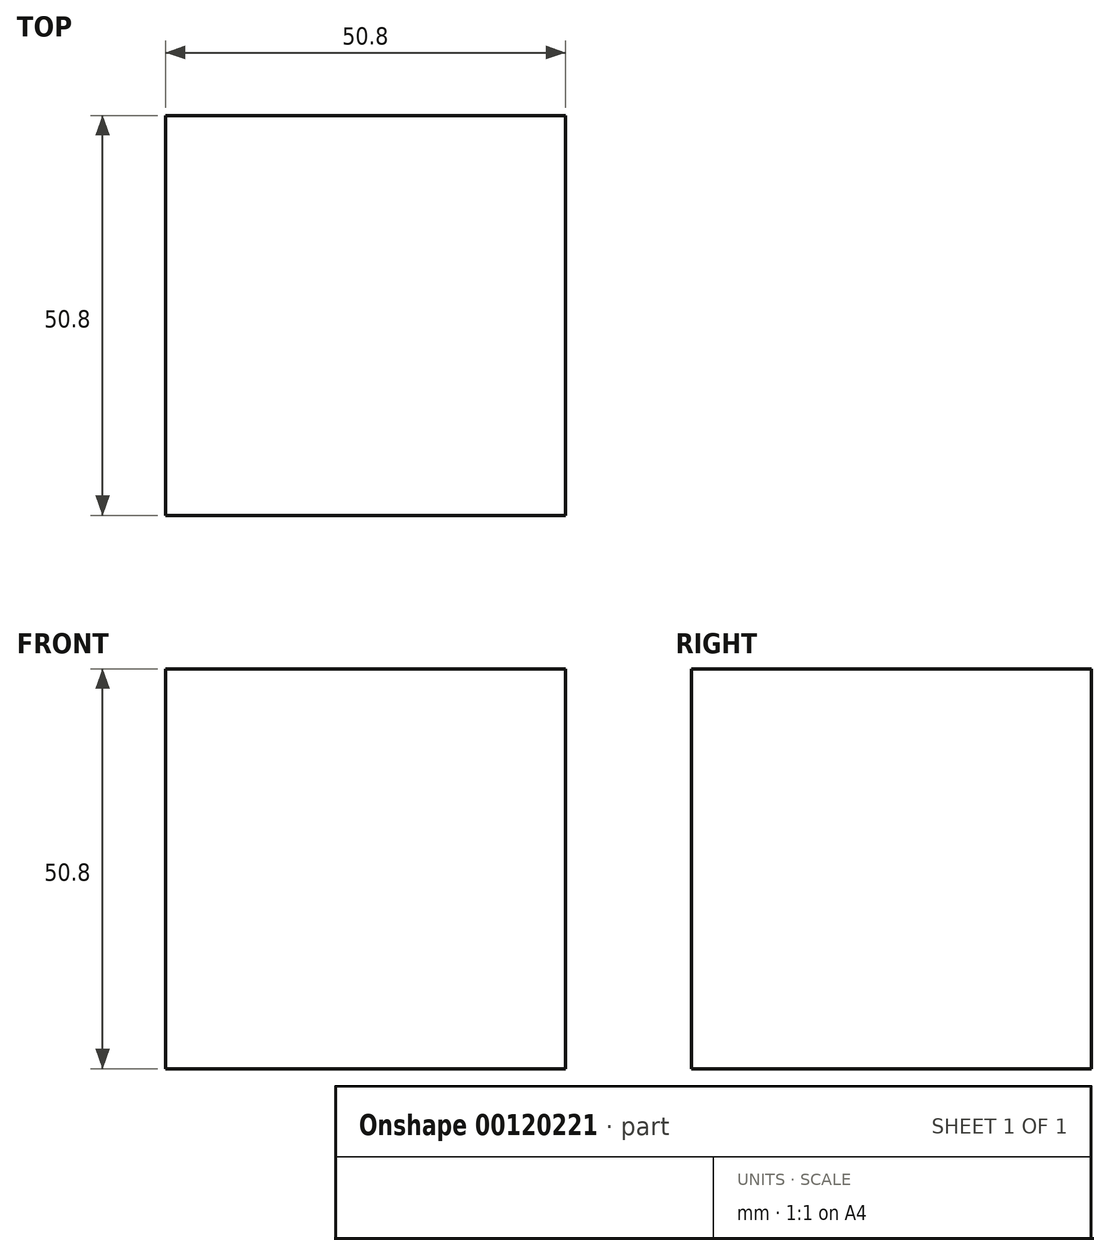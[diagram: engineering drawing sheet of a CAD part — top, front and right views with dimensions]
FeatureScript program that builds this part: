
annotation { "Feature Type Name" : "Feature", "Feature Type Description" : "" }
export const myFeature = defineFeature(function(context is Context, id is Id, definition is map)
    precondition{}
    {
        {
            var Q0;
            Q0=qCreatedBy(makeId("Top.planeOp"),FACE);
            var sketch = newSketch(context, id + "F0", { "sketchPlane" : qUnion([Q0])});
            skLineSegment(sketch, "E0.bottom", {"start": v(-20.33, 28.96) * mm, "end": v(30.47, 28.96) * mm});
            skLineSegment(sketch, "E0.top", {"start": v(-20.33, -21.84) * mm, "end": v(30.47, -21.84) * mm});
            skLineSegment(sketch, "E0.left", {"start": v(-20.33, 28.96) * mm, "end": v(-20.33, -21.84) * mm});
            skLineSegment(sketch, "E0.right", {"start": v(30.47, 28.96) * mm, "end": v(30.47, -21.84) * mm});
            skSolve(sketch);
        }
        {
            var Q0;
            Q0 = qSketchRegion(id + "F0", true);
            extrude(context, id + "F1", {"entities" : qUnion([Q0]), "depth" : 50.8 * mm});
        }
    });
